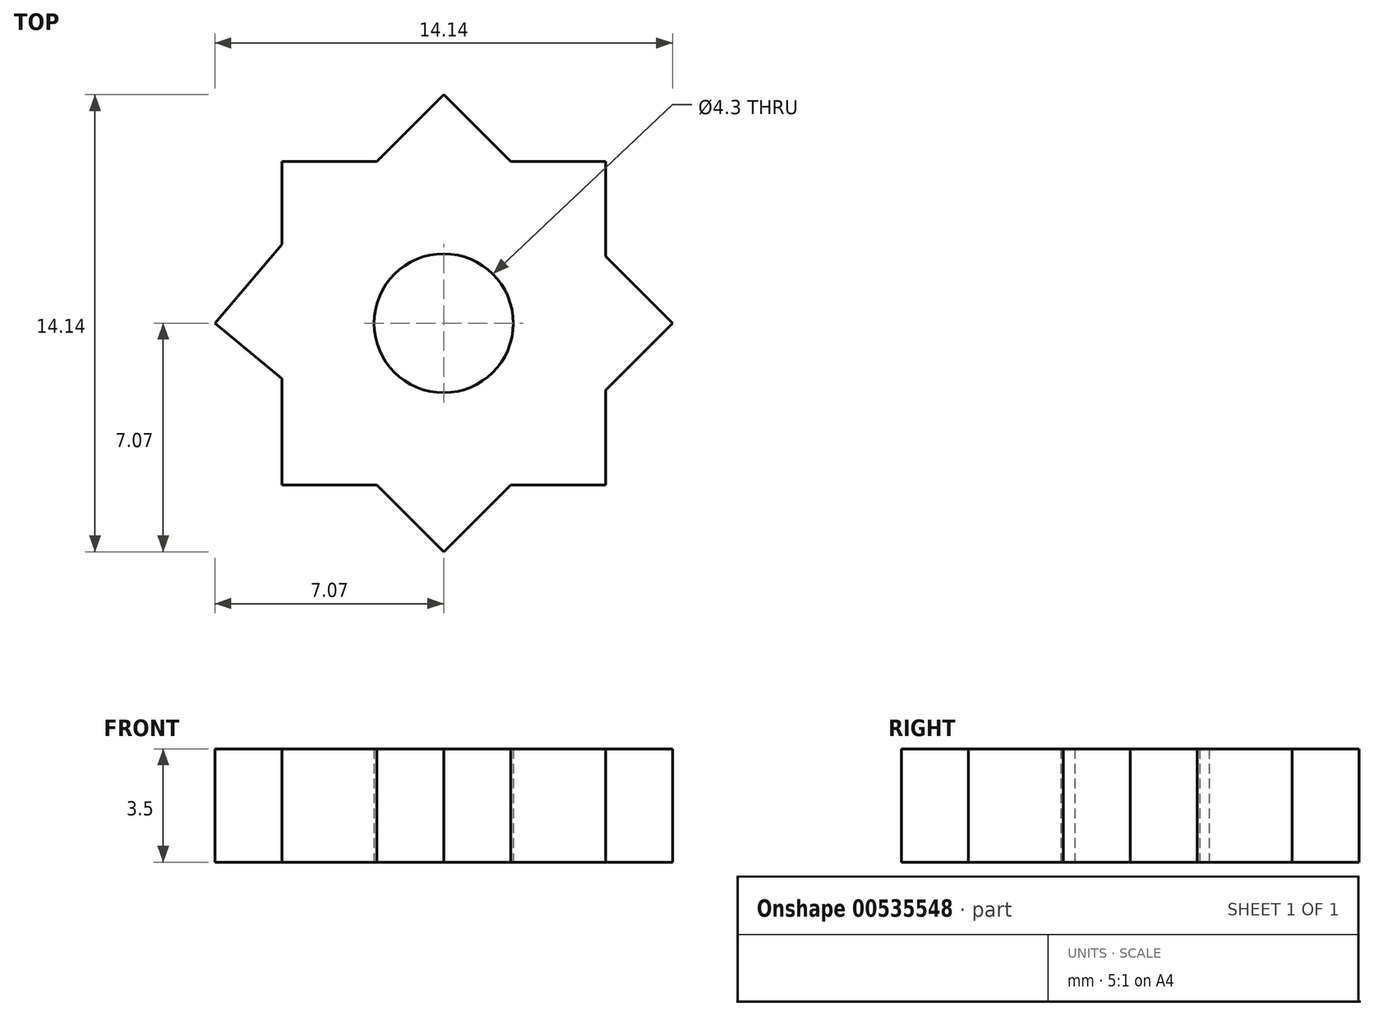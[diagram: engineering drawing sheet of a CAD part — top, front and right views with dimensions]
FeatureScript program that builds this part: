
annotation { "Feature Type Name" : "Feature", "Feature Type Description" : "" }
export const myFeature = defineFeature(function(context is Context, id is Id, definition is map)
    precondition{}
    {
        {
            var Q0;
            Q0=qCreatedBy(makeId("Top.planeOp"),FACE);
            var sketch = newSketch(context, id + "F0", { "sketchPlane" : qUnion([Q0])});
            skCircle(sketch, "E0", {"center": v(0, 0) * mm, "radius": 2.15 * mm});
            skCircle(sketch, "E1", {"center": v(0, 0) * mm, "radius": 5 * mm});
            skLineSegment(sketch, "E2", {"start": v(-5, 5) * mm, "end": v(-2.07, 5) * mm});
            skLineSegment(sketch, "E3", {"start": v(-2.07, 5) * mm, "end": v(0, 7.07) * mm});
            skLineSegment(sketch, "E4", {"start": v(0, 7.07) * mm, "end": v(2.07, 5) * mm});
            skLineSegment(sketch, "E5", {"start": v(2.07, 5) * mm, "end": v(5, 5) * mm});
            skLineSegment(sketch, "E6", {"start": v(5, 5) * mm, "end": v(5, 2.07) * mm});
            skLineSegment(sketch, "E7", {"start": v(5, 2.07) * mm, "end": v(7.07, 0) * mm});
            skLineSegment(sketch, "E8", {"start": v(7.07, 0) * mm, "end": v(5, -2.07) * mm});
            skLineSegment(sketch, "E9", {"start": v(5, -2.07) * mm, "end": v(5, -5) * mm});
            skLineSegment(sketch, "E10", {"start": v(5, -5) * mm, "end": v(2.07, -5) * mm});
            skLineSegment(sketch, "E11", {"start": v(2.07, -5) * mm, "end": v(0, -7.07) * mm});
            skLineSegment(sketch, "E12", {"start": v(0, -7.07) * mm, "end": v(-2.07, -5) * mm});
            skLineSegment(sketch, "E13", {"start": v(-2.07, -5) * mm, "end": v(-5, -5) * mm});
            skLineSegment(sketch, "E14", {"start": v(-5, -5) * mm, "end": v(-5, -1.7) * mm});
            skLineSegment(sketch, "E15", {"start": v(-5, -1.7) * mm, "end": v(-7.07, 0) * mm});
            skLineSegment(sketch, "E16", {"start": v(-7.07, 0) * mm, "end": v(-5, 2.43) * mm});
            skLineSegment(sketch, "E17", {"start": v(-5, 2.43) * mm, "end": v(-5, 5) * mm});
            skSolve(sketch);
        }
        {
            var Q0;
            Q0 = qSketchRegion(id + "F0", true);
            var Q1;
            Q1=makeQuery(id+"F0.imprint","IMPRINT",FACE,{"disambiguationData":[TD([[makeQuery(id+"F0.imprint","IMPRINT",EDGE,{"derivedFrom":sQuery(id+"F0.wireOp",EDGE,"E0")}),-1.0]])]});
            extrude(context, id + "F1", {"entities" : qUnion([Q0, Q1]), "depth" : 3.5 * mm, "offsetDistance" : 25 * mm});
        }
    });
